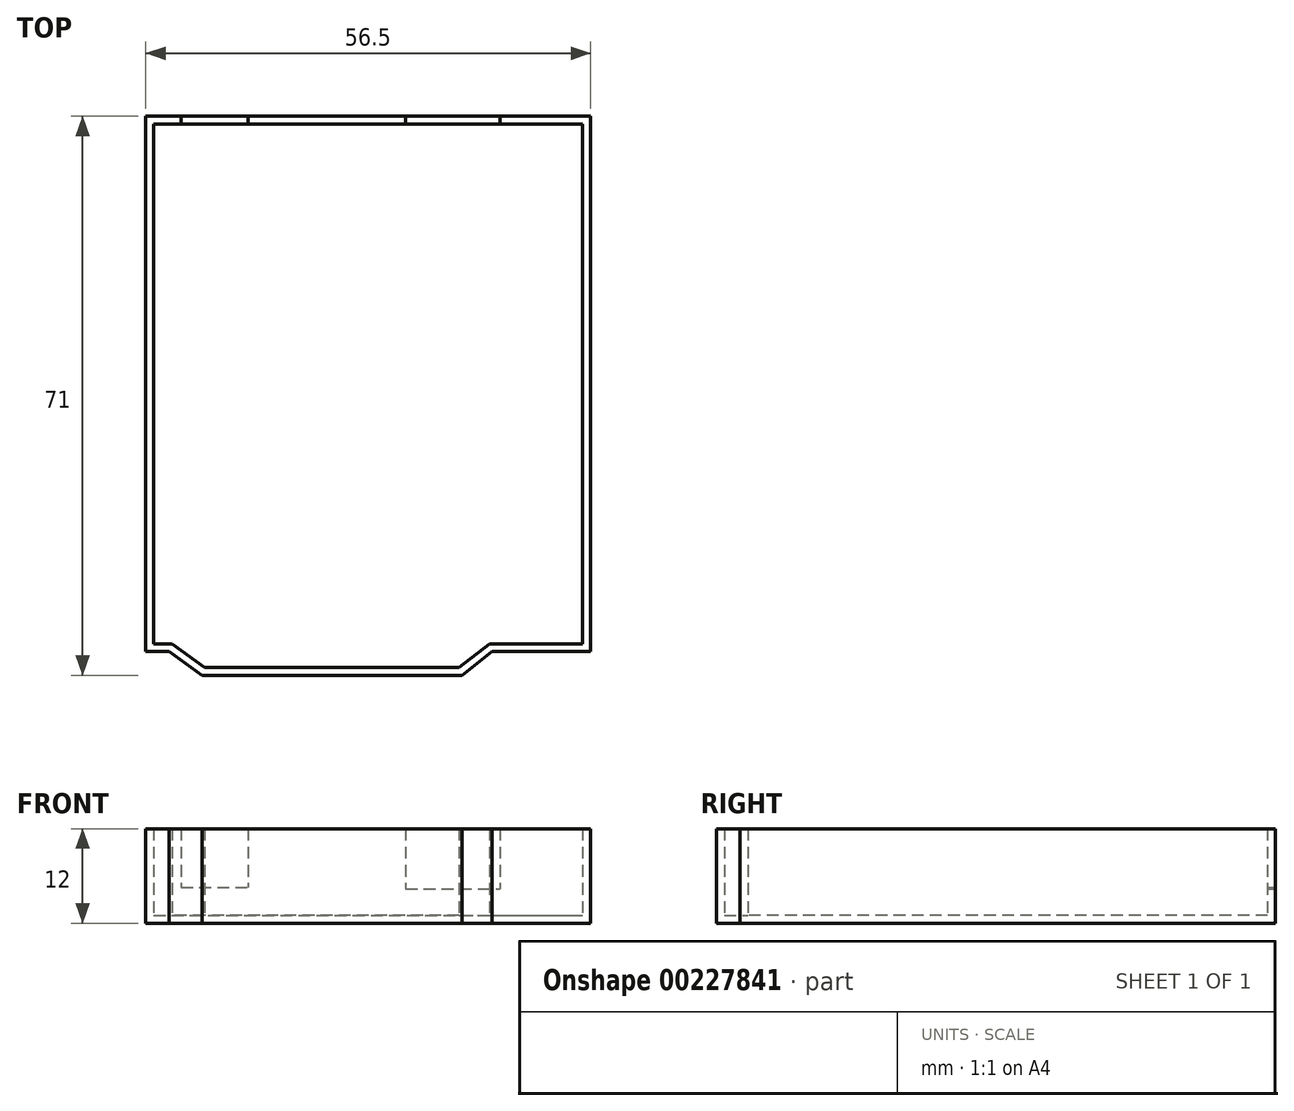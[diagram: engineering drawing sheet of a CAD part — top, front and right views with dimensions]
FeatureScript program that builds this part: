
annotation { "Feature Type Name" : "Feature", "Feature Type Description" : "" }
export const myFeature = defineFeature(function(context is Context, id is Id, definition is map)
    precondition{}
    {
        {
            var Q0;
            Q0=qCreatedBy(makeId("Top.planeOp"),FACE);
            var sketch = newSketch(context, id + "F0", { "sketchPlane" : qUnion([Q0])});
            skLineSegment(sketch, "E0.bottom", {"start": v(-28.25, 34) * mm, "end": v(28.25, 34) * mm});
            skLineSegment(sketch, "E0.top", {"start": v(-28.25, -34) * mm, "end": v(28.25, -34) * mm});
            skLineSegment(sketch, "E0.left", {"start": v(-28.25, 34) * mm, "end": v(-28.25, -34) * mm});
            skLineSegment(sketch, "E0.right", {"start": v(28.25, 34) * mm, "end": v(28.25, -34) * mm});
            skPoint(sketch, "E0.middle", {"position": v(0, 0) * mm});
            skLineSegment(sketch, "E1", {"start": v(11.92, -37) * mm, "end": v(-21.08, -37) * mm});
            skLineSegment(sketch, "E2", {"start": v(-21.08, -37) * mm, "end": v(-25.25, -34) * mm});
            skLineSegment(sketch, "E3", {"start": v(11.92, -37) * mm, "end": v(15.75, -34) * mm});
            skSolve(sketch);
        }
        {
            var Q0;
            Q0=makeQuery(id+"F0.imprint","IMPRINT",FACE,{"disambiguationData":[TD([[makeQuery(id+"F0.imprint","IMPRINT",EDGE,{"derivedFrom":sQuery(id+"F0.wireOp",EDGE,"E0.bottom")}),-1.0]])]});
            var Q1;
            Q1=makeQuery(id+"F0.imprint","IMPRINT",FACE,{"disambiguationData":[TD([[makeQuery(id+"F0.imprint","IMPRINT",EDGE,{"derivedFrom":sQuery(id+"F0.wireOp",EDGE,"E1")}),-1.0]])]});
            var Q2;
            Q2=sQuery(id+"F0.wireOp",EDGE,"E0.right");
            var Q3;
            Q3=sQuery(id+"F0.wireOp",EDGE,"E1");
            var Q4;
            Q4=sQuery(id+"F0.wireOp",EDGE,"E3");
            var Q5;
            Q5=sQuery(id+"F0.wireOp",EDGE,"E2");
            var Q6;
            Q6=sQuery(id+"F0.wireOp",EDGE,"E0.top");
            var Q7;
            Q7=sQuery(id+"F0.wireOp",EDGE,"E0.left");
            var Q8;
            Q8=sQuery(id+"F0.wireOp",EDGE,"E0.bottom");
            extrude(context, id + "F1", {"entities" : qUnion([Q0, Q1]), "surfaceEntities" : qUnion([Q2, Q3, Q4, Q5, Q6, Q7, Q8]), "depth" : 12 * mm});
        }
        {
            var Q0;
            Q0=makeQuery(id+"F1.opExtrude","CAP_FACE",FACE,{"disambiguationData":[OSD([sQuery(id+"F0.wireOp",EDGE,"E0.bottom"),sQuery(id+"F0.wireOp",EDGE,"E0.top"),sQuery(id+"F0.wireOp",EDGE,"E0.left"),sQuery(id+"F0.wireOp",EDGE,"E0.right"),sQuery(id+"F0.wireOp",EDGE,"E1"),sQuery(id+"F0.wireOp",EDGE,"E2"),sQuery(id+"F0.wireOp",EDGE,"E3"),sQuery(id+"F0.wireOp",EDGE,"g8Oaoxmu-qkdm-4w2W-jrd0-EjpGlcM1s0Rg"),sQuery(id+"F0.wireOp",EDGE,"puaTR1j5-s9Xw-CdXG-MdMp-hB1wwmCeDVNL")])],"isStart":false});
            shell(context, id + "F2", {"entities" : qUnion([Q0]), "thickness" : 1 * mm});
        }
        {
            var Q0;
            Q0=qCreatedBy(makeId("Front.planeOp"),FACE);
            cPlane(context, id + "F3", {"entities" : qUnion([Q0]), "cplaneType" : CPlaneType.OFFSET, "offset" : 34 * mm, "oppositeDirection" : true, "width" : 150 * mm, "height" : 150 * mm});
        }
        {
            var Q0;
            Q0=qCreatedBy(id+"F3.planeOp",FACE);
            var sketch = newSketch(context, id + "F4", { "sketchPlane" : qUnion([Q0])});
            skLineSegment(sketch, "E4.bottom", {"start": v(-23.75, 15.54) * mm, "end": v(-15.25, 15.54) * mm});
            skLineSegment(sketch, "E4.top", {"start": v(-23.75, 4.54) * mm, "end": v(-15.25, 4.54) * mm});
            skLineSegment(sketch, "E4.left", {"start": v(-23.75, 15.54) * mm, "end": v(-23.75, 4.54) * mm});
            skLineSegment(sketch, "E4.right", {"start": v(-15.25, 15.54) * mm, "end": v(-15.25, 4.54) * mm});
            skLineSegment(sketch, "E5.bottom", {"start": v(4.75, 15.38) * mm, "end": v(16.75, 15.38) * mm});
            skLineSegment(sketch, "E5.top", {"start": v(4.75, 4.38) * mm, "end": v(16.75, 4.38) * mm});
            skLineSegment(sketch, "E5.left", {"start": v(4.75, 15.38) * mm, "end": v(4.75, 4.38) * mm});
            skLineSegment(sketch, "E5.right", {"start": v(16.75, 15.38) * mm, "end": v(16.75, 4.38) * mm});
            skSolve(sketch);
        }
        {
            var Q0;
            Q0=makeQuery(id+"F4.imprint","IMPRINT",FACE,{"disambiguationData":[TD([[makeQuery(id+"F4.imprint","IMPRINT",EDGE,{"derivedFrom":sQuery(id+"F4.wireOp",EDGE,"E5.bottom")}),-1.0]])]});
            var Q1;
            Q1=makeQuery(id+"F4.imprint","IMPRINT",FACE,{"disambiguationData":[TD([[makeQuery(id+"F4.imprint","IMPRINT",EDGE,{"derivedFrom":sQuery(id+"F4.wireOp",EDGE,"E4.bottom")}),-1.0]])]});
            extrude(context, id + "F5", {"entities" : qUnion([Q0, Q1]), "operationType" : NewBodyOperationType.REMOVE, "depth" : 5 * mm});
        }
    });
